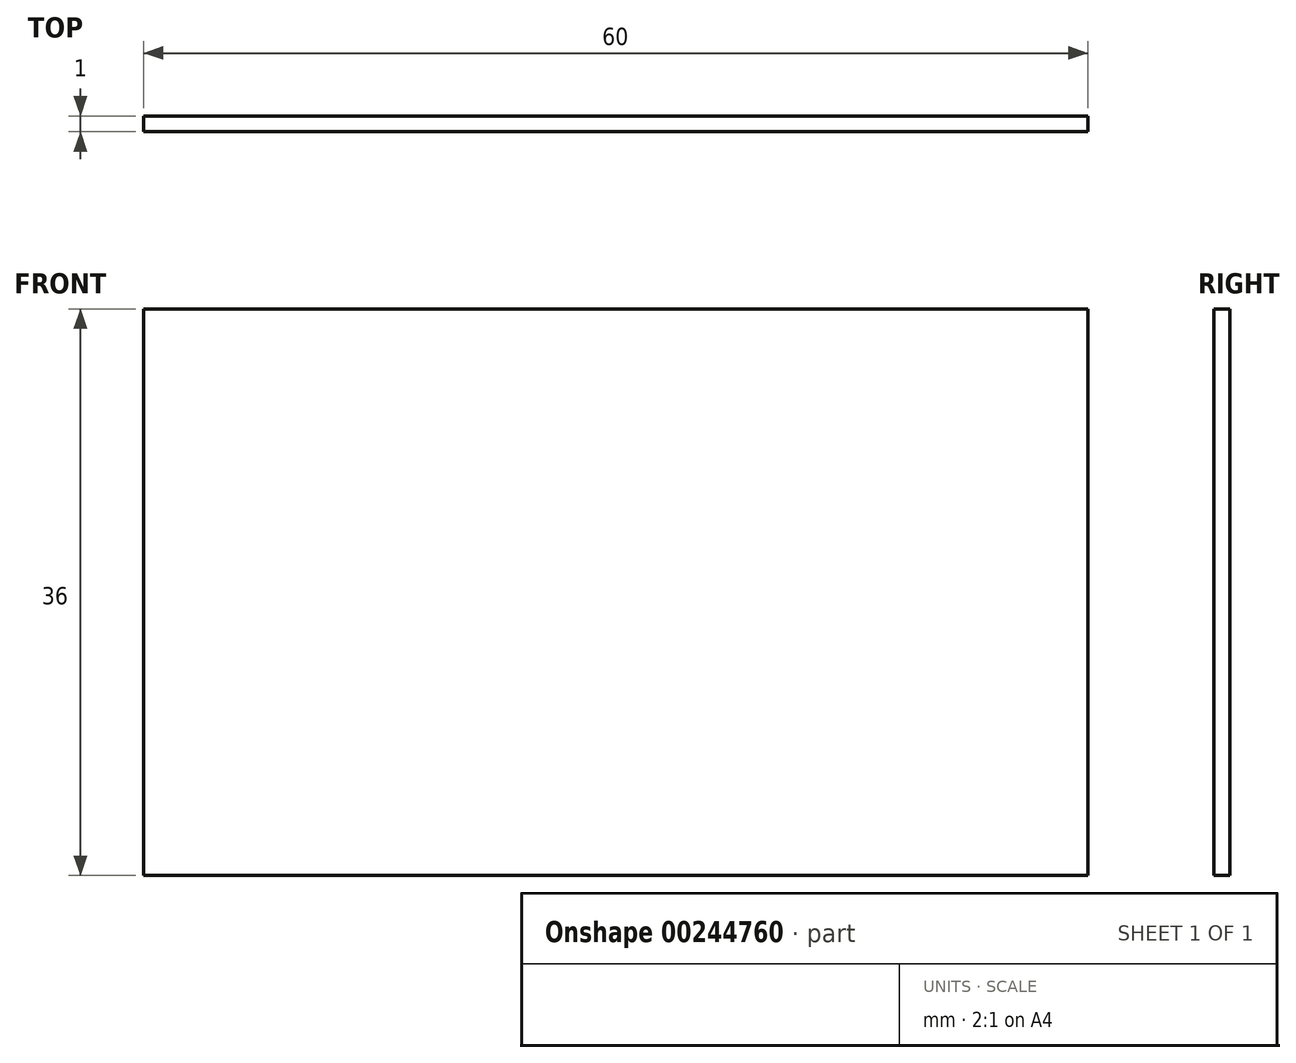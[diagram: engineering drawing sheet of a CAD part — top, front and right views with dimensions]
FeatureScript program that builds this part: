
annotation { "Feature Type Name" : "Feature", "Feature Type Description" : "" }
export const myFeature = defineFeature(function(context is Context, id is Id, definition is map)
    precondition{}
    {
        {
            var Q0;
            Q0=qCreatedBy(makeId("Front.planeOp"),FACE);
            var sketch = newSketch(context, id + "F0", { "sketchPlane" : qUnion([Q0])});
            skLineSegment(sketch, "E0.bottom", {"start": v(-43.9, 42.77) * mm, "end": v(16.1, 42.77) * mm});
            skLineSegment(sketch, "E0.top", {"start": v(-43.9, 6.77) * mm, "end": v(16.1, 6.77) * mm});
            skLineSegment(sketch, "E0.left", {"start": v(-43.9, 42.77) * mm, "end": v(-43.9, 6.77) * mm});
            skLineSegment(sketch, "E0.right", {"start": v(16.1, 42.77) * mm, "end": v(16.1, 6.77) * mm});
            skSolve(sketch);
        }
        {
            var Q0;
            Q0=makeQuery(id+"F0.imprint","IMPRINT",FACE,{"disambiguationData":[TD([[makeQuery(id+"F0.imprint","IMPRINT",EDGE,{"derivedFrom":sQuery(id+"F0.wireOp",EDGE,"E0.bottom")}),-1.0]])]});
            extrude(context, id + "F1", {"entities" : qUnion([Q0]), "depth" : 1 * mm});
        }
    });
